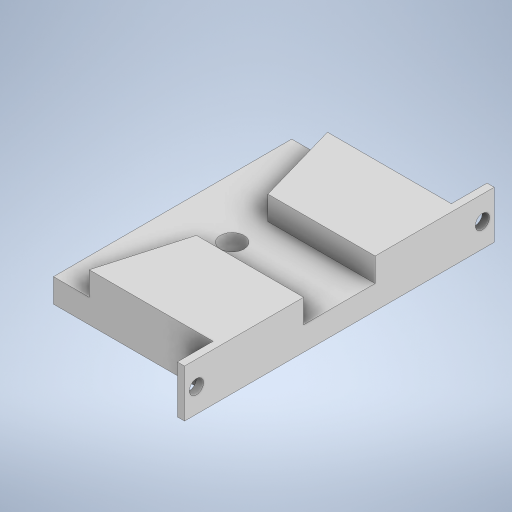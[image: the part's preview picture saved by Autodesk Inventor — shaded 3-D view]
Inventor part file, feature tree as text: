
AUTODESK INVENTOR PART (.ipt)
format: ipt  version: 2023 (Build 270158000, 158)  size: 292,352 bytes
history: native  units: mm
features: extrude x5, sketch x4, other x1, chamfer x1
ambient origin geometry x8: Origin, YZ Plane, XZ Plane, XY Plane, X Axis, Y Axis, Z Axis, Center Point
bodies: Body1 (feature_tree)
feature tree (11):
  other  "Твердое тело1"
  extrude  "Выдавливание1"  Depth=70.0mm
  sketch  "Эскиз2"
  extrude  "Выдавливание2"  Depth=100.0mm
  extrude  "Выдавливание3"  Depth=10.0mm TaperAngle=0.0deg
  extrude  "Выдавливание4"  Depth=45.0mm
  chamfer  "Фаска1"  Distance=10.0mm
  extrude  "Выдавливание5"  Depth=15.0mm
  sketch  "Эскиз1"
  sketch  "Эскиз3"
  sketch  "Эскиз4"
